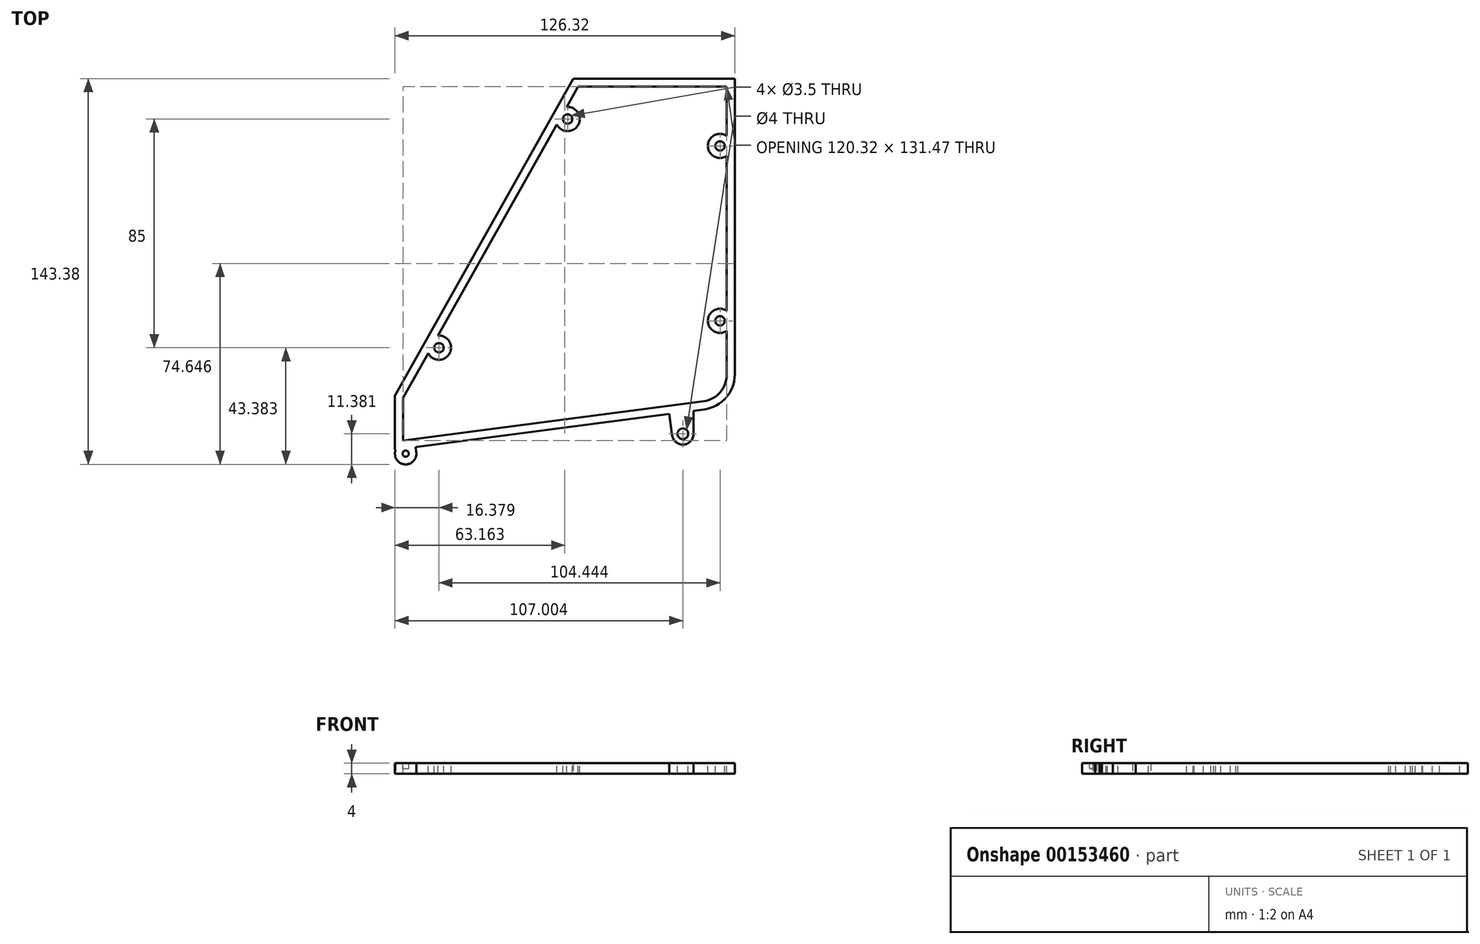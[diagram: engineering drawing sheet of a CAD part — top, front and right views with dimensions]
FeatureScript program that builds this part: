
annotation { "Feature Type Name" : "Feature", "Feature Type Description" : "" }
export const myFeature = defineFeature(function(context is Context, id is Id, definition is map)
    precondition{}
    {
        {
            var Q0;
            Q0=qCreatedBy(makeId("Top.planeOp"),FACE);
            var sketch = newSketch(context, id + "F0", { "sketchPlane" : qUnion([Q0])});
            skLineSegment(sketch, "E0", {"start": v(-60.03, 83.64) * mm, "end": v(-60.03, -26.36) * mm});
            skLineSegment(sketch, "E1", {"start": v(-48.72, -39.25) * mm, "end": v(66.28, -54.25) * mm});
            skLineSegment(sketch, "E2", {"start": v(66.28, -34.25) * mm, "end": v(-0.03, 83.64) * mm});
            skLineSegment(sketch, "E3", {"start": v(-60.03, 83.64) * mm, "end": v(-0.03, 83.64) * mm});
            skLineSegment(sketch, "E4", {"start": v(66.28, -34.25) * mm, "end": v(66.28, -54.25) * mm});
            skPoint(sketch, "E5.visualSharp", {"position": v(-60.03, -37.77) * mm});
            skArc(sketch, "E5.filletArc", {"start": v(-60.03, -26.36) * mm, "mid": v(-56.8, -34.93) * mm, "end": v(-48.72, -39.25) * mm});
            skCircle(sketch, "E6", {"center": v(62.28, -55.74) * mm, "radius": 4 * mm});
            skLineSegment(sketch, "E7", {"start": v(66.28, -55.79) * mm, "end": v(66.28, -54.25) * mm});
            skLineSegment(sketch, "E8", {"start": v(58.37, -54.91) * mm, "end": v(58.59, -53.24) * mm});
            skCircle(sketch, "E9", {"center": v(-40.72, -48.36) * mm, "radius": 4 * mm});
            skLineSegment(sketch, "E10", {"start": v(-44.71, -48.48) * mm, "end": v(-44.71, -39.77) * mm});
            skLineSegment(sketch, "E11", {"start": v(-36.75, -48.88) * mm, "end": v(-35.72, -40.94) * mm});
            skSolve(sketch);
        }
        {
            var Q0;
            {var subQ0=sQuery(id+"F0.wireOp",EDGE,"E7");var subQ1=sQuery(id+"F0.wireOp",EDGE,"E6");var subQ2=makeQuery(id+"F0.imprint","INTERSECT",VERTEX,{"disambiguationData":[OD(0.0)],"derivedFrom":[subQ1,subQ0]});Q0=makeQuery(id+"F0.imprint","IMPRINT",FACE,{"disambiguationData":[TD([[makeQuery(id+"F0.imprint","IMPRINT",EDGE,{"disambiguationData":[TD([[subQ2,-1.0]])],"derivedFrom":subQ1}),1.0]])]});}
            var Q1;
            {var subQ0=sQuery(id+"F0.wireOp",EDGE,"E10");var subQ1=sQuery(id+"F0.wireOp",EDGE,"E9");var subQ2=makeQuery(id+"F0.imprint","INTERSECT",VERTEX,{"disambiguationData":[OD(0.0)],"derivedFrom":[subQ1,subQ0]});Q1=makeQuery(id+"F0.imprint","IMPRINT",FACE,{"disambiguationData":[TD([[makeQuery(id+"F0.imprint","IMPRINT",EDGE,{"disambiguationData":[TD([[subQ2,1.0]])],"derivedFrom":subQ1}),1.0]])]});}
            var Q2;
            {var subQ0=sQuery(id+"F0.wireOp",EDGE,"E10");var subQ1=sQuery(id+"F0.wireOp",EDGE,"E1");var subQ2=makeQuery(id+"F0.imprint","INTERSECT",VERTEX,{"derivedFrom":[subQ1,subQ0]});Q2=makeQuery(id+"F0.imprint","IMPRINT",FACE,{"disambiguationData":[TD([[makeQuery(id+"F0.imprint","IMPRINT",EDGE,{"disambiguationData":[TD([[subQ2,-1.0]])],"derivedFrom":subQ1}),-1.0]])]});}
            var Q3;
            {var subQ0=sQuery(id+"F0.wireOp",EDGE,"E11");Q3=makeQuery(id+"F0.imprint","IMPRINT",FACE,{"disambiguationData":[TD([[makeQuery(id+"F0.imprint","IMPRINT",EDGE,{"derivedFrom":subQ0}),1.0]])]});}
            var Q4;
            {var subQ0=sQuery(id+"F0.wireOp",EDGE,"E8");Q4=makeQuery(id+"F0.imprint","IMPRINT",FACE,{"disambiguationData":[TD([[makeQuery(id+"F0.imprint","IMPRINT",EDGE,{"derivedFrom":subQ0}),-1.0]])]});}
            var Q5;
            {var subQ0=sQuery(id+"F0.wireOp",EDGE,"E7");var subQ3=sQuery(id+"F0.wireOp",EDGE,"E6");var subQ5=makeQuery(id+"F0.imprint","INTERSECT",VERTEX,{"disambiguationData":[OD(1.0)],"derivedFrom":[subQ3,subQ0]});Q5=makeQuery(id+"F0.imprint","IMPRINT",FACE,{"disambiguationData":[TD([[makeQuery(id+"F0.imprint","IMPRINT",EDGE,{"disambiguationData":[TD([[subQ5,-1.0]])],"derivedFrom":subQ3}),-1.0]])]});}
            var Q6;
            {var subQ0=sQuery(id+"F0.wireOp",EDGE,"E9");var subQ2=sQuery(id+"F0.wireOp",EDGE,"E1");var subQ7=makeQuery(id+"F0.imprint","INTERSECT",VERTEX,{"disambiguationData":[OD(0.0)],"derivedFrom":[subQ2,subQ0]});Q6=makeQuery(id+"F0.imprint","IMPRINT",FACE,{"disambiguationData":[TD([[makeQuery(id+"F0.imprint","IMPRINT",EDGE,{"disambiguationData":[TD([[subQ7,-1.0]])],"derivedFrom":subQ2}),-1.0]])]});}
            var Q7;
            {var subQ1=sQuery(id+"F0.wireOp",EDGE,"E6");var subQ4=sQuery(id+"F0.wireOp",EDGE,"E1");var subQ5=makeQuery(id+"F0.imprint","INTERSECT",VERTEX,{"disambiguationData":[OD(0.0)],"derivedFrom":[subQ4,subQ1]});Q7=makeQuery(id+"F0.imprint","IMPRINT",FACE,{"disambiguationData":[TD([[makeQuery(id+"F0.imprint","IMPRINT",EDGE,{"disambiguationData":[TD([[subQ5,-1.0]])],"derivedFrom":subQ4}),-1.0]])]});}
            var Q8;
            {var subQ0=sQuery(id+"F0.wireOp",EDGE,"E6");var subQ1=sQuery(id+"F0.wireOp",EDGE,"E1");var subQ2=makeQuery(id+"F0.imprint","INTERSECT",VERTEX,{"disambiguationData":[OD(0.0)],"derivedFrom":[subQ1,subQ0]});Q8=makeQuery(id+"F0.imprint","IMPRINT",FACE,{"disambiguationData":[TD([[makeQuery(id+"F0.imprint","IMPRINT",EDGE,{"disambiguationData":[TD([[subQ2,-1.0]])],"derivedFrom":subQ1}),1.0]])]});}
            var Q9;
            Q9=makeQuery(id+"F0.imprint","IMPRINT",FACE,{"disambiguationData":[TD([[makeQuery(id+"F0.imprint","IMPRINT",EDGE,{"derivedFrom":sQuery(id+"F0.wireOp",EDGE,"E0")}),1.0]])]});
            var Q10;
            {var subQ0=sQuery(id+"F0.wireOp",EDGE,"E9");var subQ1=sQuery(id+"F0.wireOp",EDGE,"E1");var subQ2=makeQuery(id+"F0.imprint","INTERSECT",VERTEX,{"disambiguationData":[OD(0.0)],"derivedFrom":[subQ1,subQ0]});Q10=makeQuery(id+"F0.imprint","IMPRINT",FACE,{"disambiguationData":[TD([[makeQuery(id+"F0.imprint","IMPRINT",EDGE,{"disambiguationData":[TD([[subQ2,-1.0]])],"derivedFrom":subQ1}),1.0]])]});}
            var Q11;
            {var subQ0=sQuery(id+"F0.wireOp",EDGE,"E10");var subQ1=sQuery(id+"F0.wireOp",EDGE,"E9");var subQ2=makeQuery(id+"F0.imprint","INTERSECT",VERTEX,{"disambiguationData":[OD(0.0)],"derivedFrom":[subQ1,subQ0]});Q11=makeQuery(id+"F0.imprint","IMPRINT",FACE,{"disambiguationData":[TD([[makeQuery(id+"F0.imprint","IMPRINT",EDGE,{"disambiguationData":[TD([[subQ2,-1.0]])],"derivedFrom":subQ1}),1.0]])]});}
            extrude(context, id + "F1", {"entities" : qUnion([Q0, Q1, Q2, Q3, Q4, Q5, Q6, Q7, Q8, Q9, Q10, Q11]), "depth" : 4 * mm});
        }
        {
            var Q0;
            Q0=makeQuery(id+"F1.opExtrude","CAP_FACE",FACE,{"disambiguationData":[OSD([sQuery(id+"F0.wireOp",EDGE,"E0"),sQuery(id+"F0.wireOp",EDGE,"E1"),sQuery(id+"F0.wireOp",EDGE,"E2"),sQuery(id+"F0.wireOp",EDGE,"E3"),sQuery(id+"F0.wireOp",EDGE,"E4"),sQuery(id+"F0.wireOp",EDGE,"E5.filletArc")])],"isStart":false});
            var sketch = newSketch(context, id + "F2", { "sketchPlane" : qUnion([Q0])});
            skLineSegment(sketch, "E12.0", {"start": v(-48.46, -37.26) * mm, "end": v(52.4, -50.42) * mm});
            skArc(sketch, "E12.1", {"start": v(-58.03, -26.36) * mm, "mid": v(-55.3, -33.61) * mm, "end": v(-48.46, -37.26) * mm});
            skLineSegment(sketch, "E12.2", {"start": v(-58.03, 83.64) * mm, "end": v(-58.03, -26.36) * mm});
            skLineSegment(sketch, "E13", {"start": v(66.28, -54.25) * mm, "end": v(66.28, -52.23) * mm});
            skLineSegment(sketch, "E14", {"start": v(-60.03, 83.64) * mm, "end": v(-58.03, 83.64) * mm});
            skLineSegment(sketch, "E15", {"start": v(-48.46, -37.26) * mm, "end": v(-48.72, -39.25) * mm});
            skLineSegment(sketch, "E16.0", {"start": v(59.2, -25.73) * mm, "end": v(-2.7, 84.31) * mm});
            skLineSegment(sketch, "E17", {"start": v(-2.33, 83.64) * mm, "end": v(-2.7, 84.31) * mm});
            skLineSegment(sketch, "E18", {"start": v(59.2, -25.73) * mm, "end": v(66.28, -34.25) * mm});
            skSolve(sketch);
        }
        {
            var Q0;
            Q0=qSketchRegion(id+"F2",true);
            var Q1;
            Q1=makeQuery(id+"F2.imprint","IMPRINT",FACE,{"disambiguationData":[TD([[makeQuery(id+"F2.imprint","IMPRINT",EDGE,{"derivedFrom":sQuery(id+"F2.wireOp",EDGE,"E12.1")}),-1.0]])]});
            var Q2;
            {var subQ2=sQuery(id+"F2.wireOp",EDGE,"E17");Q2=makeQuery(id+"F2.imprint","IMPRINT",FACE,{"disambiguationData":[TD([[makeQuery(id+"F2.imprint","IMPRINT",EDGE,{"derivedFrom":subQ2}),-1.0]])]});}
            var Q3;
            {var subQ0=sQuery(id+"F2.wireOp",EDGE,"E16.0");Q3=makeQuery(id+"F2.imprint","IMPRINT",FACE,{"disambiguationData":[TD([[makeQuery(id+"F2.imprint","IMPRINT",EDGE,{"derivedFrom":subQ0}),-1.0]])]});}
            extrude(context, id + "F3", {"entities" : qUnion([Q0, Q1, Q2, Q3]), "operationType" : NewBodyOperationType.ADD, "depth" : 55 * mm});
        }
        {
            var Q0;
            {var subQ0=sQuery(id+"F0.wireOp",EDGE,"E0");Q0=makeQuery(id+"F3.boolean.opBoolean","MERGE",FACE,{"derivedFrom":[makeQuery(id+"F1.opExtrude","SWEPT_FACE",FACE,{"disambiguationData":[OSD([subQ0])]}),makeQuery(id+"F3.opExtrude","SWEPT_FACE",FACE,{"disambiguationData":[OSD([subQ0])]})]});}
            var sketch = newSketch(context, id + "F4", { "sketchPlane" : qUnion([Q0])});
            skCircle(sketch, "E19", {"center": v(23.36, 41.5) * mm, "radius": 2.5 * mm});
            skCircle(sketch, "E20", {"center": v(-74.64, 41.5) * mm, "radius": 2.5 * mm});
            skSolve(sketch);
        }
        {
            var Q0;
            Q0=qSketchRegion(id+"F4",true);
            extrude(context, id + "F5", {"entities" : qUnion([Q0]), "operationType" : NewBodyOperationType.REMOVE, "endBound" : BoundingType.UP_TO_NEXT, "oppositeDirection" : true, "depth" : 25 * mm});
        }
        {
            var Q0;
            Q0=makeQuery(id+"F1.opExtrude","CAP_FACE",FACE,{"disambiguationData":[OSD([sQuery(id+"F0.wireOp",EDGE,"E0"),sQuery(id+"F0.wireOp",EDGE,"E1"),sQuery(id+"F0.wireOp",EDGE,"E2"),sQuery(id+"F0.wireOp",EDGE,"E3"),sQuery(id+"F0.wireOp",EDGE,"E4"),sQuery(id+"F0.wireOp",EDGE,"E5.filletArc"),sQuery(id+"F0.wireOp",EDGE,"E6"),sQuery(id+"F0.wireOp",EDGE,"E7"),sQuery(id+"F0.wireOp",EDGE,"E8")])],"isStart":false});
            var sketch = newSketch(context, id + "F6", { "sketchPlane" : qUnion([Q0])});
            skCircle(sketch, "E21", {"center": v(62.28, -55.74) * mm, "radius": 1.15 * mm});
            skSolve(sketch);
        }
        {
            var Q0;
            Q0=qSketchRegion(id+"F6",true);
            extrude(context, id + "F7", {"entities" : qUnion([Q0]), "operationType" : NewBodyOperationType.REMOVE, "oppositeDirection" : true, "depth" : 2 * mm});
        }
        {
            var Q0;
            Q0=makeQuery(id+"F3.opExtrude","CAP_FACE",FACE,{"disambiguationData":[OSD([sQuery(id+"F0.wireOp",EDGE,"E0"),sQuery(id+"F0.wireOp",EDGE,"E5.filletArc"),sQuery(id+"F2.wireOp",EDGE,"E12.1"),sQuery(id+"F2.wireOp",EDGE,"E12.2"),sQuery(id+"F2.wireOp",EDGE,"E14"),sQuery(id+"F2.wireOp",EDGE,"E15")])],"isStart":false});
            var sketch = newSketch(context, id + "F8", { "sketchPlane" : qUnion([Q0])});
            skCircle(sketch, "E22", {"center": v(-54.53, -6.36) * mm, "radius": 3.5 * mm});
            skLineSegment(sketch, "E23", {"start": v(-51.48, -4.64) * mm, "end": v(-58.03, 5.64) * mm});
            skLineSegment(sketch, "E24", {"start": v(-52.77, -9.38) * mm, "end": v(-58.03, -12.36) * mm});
            skCircle(sketch, "E25", {"center": v(-54.53, 58.64) * mm, "radius": 3.5 * mm});
            skLineSegment(sketch, "E26", {"start": v(-51.64, 60.61) * mm, "end": v(-58.03, 70.64) * mm});
            skLineSegment(sketch, "E27", {"start": v(-53.23, 55.4) * mm, "end": v(-58.03, 53.64) * mm});
            skSolve(sketch);
        }
        {
            var Q0;
            Q0=qSketchRegion(id+"F8",true);
            var Q1;
            {var subQ0=sQuery(id+"F8.wireOp",EDGE,"E23");Q1=makeQuery(id+"F8.imprint","IMPRINT",FACE,{"disambiguationData":[TD([[makeQuery(id+"F8.imprint","IMPRINT",EDGE,{"derivedFrom":subQ0}),1.0]])]});}
            var Q2;
            {var subQ0=sQuery(id+"F8.wireOp",EDGE,"E24");Q2=makeQuery(id+"F8.imprint","IMPRINT",FACE,{"disambiguationData":[TD([[makeQuery(id+"F8.imprint","IMPRINT",EDGE,{"derivedFrom":subQ0}),-1.0]])]});}
            var Q3;
            {var subQ0=sQuery(id+"F8.wireOp",EDGE,"E26");Q3=makeQuery(id+"F8.imprint","IMPRINT",FACE,{"disambiguationData":[TD([[makeQuery(id+"F8.imprint","IMPRINT",EDGE,{"derivedFrom":subQ0}),1.0]])]});}
            var Q4;
            {var subQ0=sQuery(id+"F8.wireOp",EDGE,"E27");var subQ1=sQuery(id+"F8.wireOp",EDGE,"E25");var subQ2=makeQuery(id+"F8.imprint","INTERSECT",VERTEX,{"disambiguationData":[OD(1.0)],"derivedFrom":[subQ1,subQ0]});Q4=makeQuery(id+"F8.imprint","IMPRINT",FACE,{"disambiguationData":[TD([[makeQuery(id+"F8.imprint","IMPRINT",EDGE,{"disambiguationData":[TD([[subQ2,1.0]])],"derivedFrom":subQ1}),-1.0]])]});}
            extrude(context, id + "F9", {"entities" : qUnion([Q0, Q1, Q2, Q3, Q4]), "operationType" : NewBodyOperationType.ADD, "oppositeDirection" : true, "depth" : 8 * mm});
        }
        {
            var Q0;
            Q0=makeQuery(id+"F3.opExtrude","CAP_FACE",FACE,{"disambiguationData":[OSD([sQuery(id+"F0.wireOp",EDGE,"E2"),sQuery(id+"F0.wireOp",EDGE,"E3"),sQuery(id+"F2.wireOp",EDGE,"E16.0"),sQuery(id+"F2.wireOp",EDGE,"E18")])],"isStart":false});
            var sketch = newSketch(context, id + "F10", { "sketchPlane" : qUnion([Q0])});
            skCircle(sketch, "E28", {"center": v(2.1, 68.64) * mm, "radius": 3.5 * mm});
            skLineSegment(sketch, "E29", {"start": v(-1.4, 68.87) * mm, "end": v(-0.64, 80.64) * mm});
            skLineSegment(sketch, "E30", {"start": v(1.24, 65.25) * mm, "end": v(8.92, 63.64) * mm});
            skCircle(sketch, "E31", {"center": v(49.9, -16.36) * mm, "radius": 3.5 * mm});
            skLineSegment(sketch, "E32", {"start": v(46.47, -15.72) * mm, "end": v(47.17, -4.36) * mm});
            skLineSegment(sketch, "E33", {"start": v(49.2, -19.78) * mm, "end": v(56.74, -21.36) * mm});
            skSolve(sketch);
        }
        {
            var Q0;
            {var subQ0=sQuery(id+"F10.wireOp",EDGE,"E32");var subQ1=sQuery(id+"F10.wireOp",EDGE,"E31");var subQ2=makeQuery(id+"F10.imprint","INTERSECT",VERTEX,{"disambiguationData":[OD(1.0)],"derivedFrom":[subQ1,subQ0]});Q0=makeQuery(id+"F10.imprint","IMPRINT",FACE,{"disambiguationData":[TD([[makeQuery(id+"F10.imprint","IMPRINT",EDGE,{"disambiguationData":[TD([[subQ2,1.0]])],"derivedFrom":subQ1}),1.0]])]});}
            var Q1;
            {var subQ0=sQuery(id+"F10.wireOp",EDGE,"E32");var subQ1=sQuery(id+"F10.wireOp",EDGE,"E31");var subQ2=makeQuery(id+"F10.imprint","INTERSECT",VERTEX,{"disambiguationData":[OD(1.0)],"derivedFrom":[subQ1,subQ0]});Q1=makeQuery(id+"F10.imprint","IMPRINT",FACE,{"disambiguationData":[TD([[makeQuery(id+"F10.imprint","IMPRINT",EDGE,{"disambiguationData":[TD([[subQ2,1.0]])],"derivedFrom":subQ1}),-1.0]])]});}
            var Q2;
            {var subQ0=sQuery(id+"F10.wireOp",EDGE,"E33");Q2=makeQuery(id+"F10.imprint","IMPRINT",FACE,{"disambiguationData":[TD([[makeQuery(id+"F10.imprint","IMPRINT",EDGE,{"derivedFrom":subQ0}),1.0]])]});}
            var Q3;
            {var subQ0=sQuery(id+"F10.wireOp",EDGE,"E28");var subQ1=makeQuery(id+"F10.imprint","INTERSECT",VERTEX,{"derivedFrom":[subQ0,sQuery(id+"F10.wireOp",EDGE,"E29")]});Q3=makeQuery(id+"F10.imprint","IMPRINT",FACE,{"disambiguationData":[TD([[makeQuery(id+"F10.imprint","IMPRINT",EDGE,{"disambiguationData":[TD([[subQ1,1.0]])],"derivedFrom":subQ0}),1.0]])]});}
            var Q4;
            {var subQ0=sQuery(id+"F10.wireOp",EDGE,"E30");var subQ1=sQuery(id+"F10.wireOp",EDGE,"E28");var subQ2=makeQuery(id+"F10.imprint","INTERSECT",VERTEX,{"disambiguationData":[OD(1.0)],"derivedFrom":[subQ1,subQ0]});Q4=makeQuery(id+"F10.imprint","IMPRINT",FACE,{"disambiguationData":[TD([[makeQuery(id+"F10.imprint","IMPRINT",EDGE,{"disambiguationData":[TD([[subQ2,-1.0]])],"derivedFrom":subQ1}),-1.0]])]});}
            var Q5;
            {var subQ0=sQuery(id+"F10.wireOp",EDGE,"E29");Q5=makeQuery(id+"F10.imprint","IMPRINT",FACE,{"disambiguationData":[TD([[makeQuery(id+"F10.imprint","IMPRINT",EDGE,{"derivedFrom":subQ0}),-1.0]])]});}
            extrude(context, id + "F11", {"entities" : qUnion([Q0, Q1, Q2, Q3, Q4, Q5]), "operationType" : NewBodyOperationType.ADD, "oppositeDirection" : true, "depth" : 7 * mm});
        }
        {
            var Q0;
            {var subQ0=sQuery(id+"F2.wireOp",EDGE,"E12.2");Q0=makeQuery(id+"F9.boolean.opBoolean","MERGE",FACE,{"derivedFrom":[makeQuery(id+"F3.opExtrude","CAP_FACE",FACE,{"disambiguationData":[OSD([sQuery(id+"F0.wireOp",EDGE,"E0"),sQuery(id+"F0.wireOp",EDGE,"E5.filletArc"),sQuery(id+"F2.wireOp",EDGE,"E12.1"),subQ0,sQuery(id+"F2.wireOp",EDGE,"E14"),sQuery(id+"F2.wireOp",EDGE,"E15")])],"isStart":false}),makeQuery(id+"F9.opExtrude","CAP_FACE",FACE,{"disambiguationData":[OSD([subQ0,sQuery(id+"F8.wireOp",EDGE,"E22"),sQuery(id+"F8.wireOp",EDGE,"E23"),sQuery(id+"F8.wireOp",EDGE,"E24")])],"isStart":true}),makeQuery(id+"F9.opExtrude","CAP_FACE",FACE,{"disambiguationData":[OSD([subQ0,sQuery(id+"F8.wireOp",EDGE,"E25"),sQuery(id+"F8.wireOp",EDGE,"E26"),sQuery(id+"F8.wireOp",EDGE,"E27")])],"isStart":true})]});}
            var sketch = newSketch(context, id + "F12", { "sketchPlane" : qUnion([Q0])});
            skCircle(sketch, "E34", {"center": v(-54.53, -6.36) * mm, "radius": 1.75 * mm});
            skCircle(sketch, "E35", {"center": v(-54.53, 58.64) * mm, "radius": 1.75 * mm});
            skSolve(sketch);
        }
        {
            var Q0;
            Q0=qSketchRegion(id+"F12",true);
            extrude(context, id + "F13", {"entities" : qUnion([Q0]), "operationType" : NewBodyOperationType.REMOVE, "endBound" : BoundingType.THROUGH_ALL, "oppositeDirection" : true, "depth" : 6.5 * mm});
        }
        {
            var Q0;
            {var subQ0=sQuery(id+"F2.wireOp",EDGE,"E16.0");Q0=makeQuery(id+"F11.boolean.opBoolean","MERGE",FACE,{"derivedFrom":[makeQuery(id+"F3.opExtrude","CAP_FACE",FACE,{"disambiguationData":[OSD([sQuery(id+"F0.wireOp",EDGE,"E2"),sQuery(id+"F0.wireOp",EDGE,"E3"),subQ0,sQuery(id+"F2.wireOp",EDGE,"E18")])],"isStart":false}),makeQuery(id+"F11.opExtrude","CAP_FACE",FACE,{"disambiguationData":[OSD([subQ0,sQuery(id+"F10.wireOp",EDGE,"E28"),sQuery(id+"F10.wireOp",EDGE,"E29"),sQuery(id+"F10.wireOp",EDGE,"E30")])],"isStart":true}),makeQuery(id+"F11.opExtrude","CAP_FACE",FACE,{"disambiguationData":[OSD([subQ0,sQuery(id+"F10.wireOp",EDGE,"E31"),sQuery(id+"F10.wireOp",EDGE,"E32"),sQuery(id+"F10.wireOp",EDGE,"E33")])],"isStart":true})]});}
            var sketch = newSketch(context, id + "F14", { "sketchPlane" : qUnion([Q0])});
            skCircle(sketch, "E36", {"center": v(49.9, -16.36) * mm, "radius": 1.75 * mm});
            skCircle(sketch, "E37", {"center": v(2.1, 68.64) * mm, "radius": 1.75 * mm});
            skSolve(sketch);
        }
        {
            var Q0;
            Q0=qSketchRegion(id+"F14",true);
            extrude(context, id + "F15", {"entities" : qUnion([Q0]), "operationType" : NewBodyOperationType.REMOVE, "endBound" : BoundingType.THROUGH_ALL, "oppositeDirection" : true, "depth" : 6.5 * mm});
        }
        {
            var Q0;
            {var subQ0=sQuery(id+"F2.wireOp",EDGE,"E12.2");Q0=makeQuery(id+"F9.boolean.opBoolean","MERGE",FACE,{"derivedFrom":[makeQuery(id+"F3.opExtrude","CAP_FACE",FACE,{"disambiguationData":[OSD([sQuery(id+"F0.wireOp",EDGE,"E0"),sQuery(id+"F0.wireOp",EDGE,"E5.filletArc"),sQuery(id+"F2.wireOp",EDGE,"E12.1"),subQ0,sQuery(id+"F2.wireOp",EDGE,"E14"),sQuery(id+"F2.wireOp",EDGE,"E15")])],"isStart":false}),makeQuery(id+"F9.opExtrude","CAP_FACE",FACE,{"disambiguationData":[OSD([subQ0,sQuery(id+"F8.wireOp",EDGE,"E22"),sQuery(id+"F8.wireOp",EDGE,"E23"),sQuery(id+"F8.wireOp",EDGE,"E24")])],"isStart":true}),makeQuery(id+"F9.opExtrude","CAP_FACE",FACE,{"disambiguationData":[OSD([subQ0,sQuery(id+"F8.wireOp",EDGE,"E25"),sQuery(id+"F8.wireOp",EDGE,"E26"),sQuery(id+"F8.wireOp",EDGE,"E27")])],"isStart":true})]});}
            extrude(context, id + "F16", {"entities" : qUnion([Q0]), "operationType" : NewBodyOperationType.REMOVE, "oppositeDirection" : true, "depth" : 55 * mm});
        }
        {
            var Q0;
            {var subQ0=sQuery(id+"F2.wireOp",EDGE,"E16.0");Q0=makeQuery(id+"F11.boolean.opBoolean","MERGE",FACE,{"derivedFrom":[makeQuery(id+"F3.opExtrude","CAP_FACE",FACE,{"disambiguationData":[OSD([sQuery(id+"F0.wireOp",EDGE,"E2"),sQuery(id+"F0.wireOp",EDGE,"E3"),subQ0,sQuery(id+"F2.wireOp",EDGE,"E18")])],"isStart":false}),makeQuery(id+"F11.opExtrude","CAP_FACE",FACE,{"disambiguationData":[OSD([subQ0,sQuery(id+"F10.wireOp",EDGE,"E28"),sQuery(id+"F10.wireOp",EDGE,"E29"),sQuery(id+"F10.wireOp",EDGE,"E30")])],"isStart":true}),makeQuery(id+"F11.opExtrude","CAP_FACE",FACE,{"disambiguationData":[OSD([subQ0,sQuery(id+"F10.wireOp",EDGE,"E31"),sQuery(id+"F10.wireOp",EDGE,"E32"),sQuery(id+"F10.wireOp",EDGE,"E33")])],"isStart":true})]});}
            var Q1;
            {var subQ0=sQuery(id+"F0.wireOp",EDGE,"E5.filletArc");var subQ1=sQuery(id+"F0.wireOp",EDGE,"E0");Q1=makeQuery(id+"F16.boolean.opBoolean","MERGE",FACE,{"derivedFrom":[makeQuery(id+"F1.opExtrude","CAP_FACE",FACE,{"disambiguationData":[OSD([subQ1,sQuery(id+"F0.wireOp",EDGE,"E1"),sQuery(id+"F0.wireOp",EDGE,"E2"),sQuery(id+"F0.wireOp",EDGE,"E3"),sQuery(id+"F0.wireOp",EDGE,"E4"),subQ0,sQuery(id+"F0.wireOp",EDGE,"E6"),sQuery(id+"F0.wireOp",EDGE,"E7"),sQuery(id+"F0.wireOp",EDGE,"E8"),sQuery(id+"F0.wireOp",EDGE,"E9"),sQuery(id+"F0.wireOp",EDGE,"E10"),sQuery(id+"F0.wireOp",EDGE,"E11")])],"isStart":false}),makeQuery(id+"F16.opExtrude","CAP_FACE",FACE,{"disambiguationData":[OSD([subQ1,subQ0,sQuery(id+"F2.wireOp",EDGE,"E12.1"),sQuery(id+"F2.wireOp",EDGE,"E12.2"),sQuery(id+"F2.wireOp",EDGE,"E14"),sQuery(id+"F2.wireOp",EDGE,"E15"),sQuery(id+"F8.wireOp",EDGE,"E22"),sQuery(id+"F8.wireOp",EDGE,"E23"),sQuery(id+"F8.wireOp",EDGE,"E24"),sQuery(id+"F8.wireOp",EDGE,"E25"),sQuery(id+"F8.wireOp",EDGE,"E26"),sQuery(id+"F8.wireOp",EDGE,"E27")])],"isStart":false})]});}
            extrude(context, id + "F17", {"entities" : qUnion([Q0]), "operationType" : NewBodyOperationType.REMOVE, "endBound" : BoundingType.UP_TO_SURFACE, "oppositeDirection" : true, "endBoundEntityFace" : qUnion([Q1]), "depth" : 55 * mm});
        }
        {
            var Q0;
            Q0=makeQuery(id+"F1.opExtrude","SWEPT_BODY",BODY,{"disambiguationData":[OSD([sQuery(id+"F0.wireOp",EDGE,"E0"),sQuery(id+"F0.wireOp",EDGE,"E1"),sQuery(id+"F0.wireOp",EDGE,"E2"),sQuery(id+"F0.wireOp",EDGE,"E3"),sQuery(id+"F0.wireOp",EDGE,"E4"),sQuery(id+"F0.wireOp",EDGE,"E5.filletArc"),sQuery(id+"F0.wireOp",EDGE,"E6"),sQuery(id+"F0.wireOp",EDGE,"E7"),sQuery(id+"F0.wireOp",EDGE,"E8"),sQuery(id+"F0.wireOp",EDGE,"E9"),sQuery(id+"F0.wireOp",EDGE,"E10"),sQuery(id+"F0.wireOp",EDGE,"E11")])]});
            var Q1;
            Q1=makeQuery(id+"F1.opExtrude","SWEPT_FACE",FACE,{"disambiguationData":[OSD([sQuery(id+"F0.wireOp",EDGE,"E4")])]});
            mirror(context, id + "F18", {"entities" : qUnion([Q0]), "mirrorPlane" : qUnion([Q1])});
        }
        {
            var Q0;
            Q0=makeQuery(id+"F1.opExtrude","SWEPT_BODY",BODY,{"disambiguationData":[OSD([sQuery(id+"F0.wireOp",EDGE,"E0"),sQuery(id+"F0.wireOp",EDGE,"E1"),sQuery(id+"F0.wireOp",EDGE,"E2"),sQuery(id+"F0.wireOp",EDGE,"E3"),sQuery(id+"F0.wireOp",EDGE,"E4"),sQuery(id+"F0.wireOp",EDGE,"E5.filletArc"),sQuery(id+"F0.wireOp",EDGE,"E6"),sQuery(id+"F0.wireOp",EDGE,"E7"),sQuery(id+"F0.wireOp",EDGE,"E8"),sQuery(id+"F0.wireOp",EDGE,"E9"),sQuery(id+"F0.wireOp",EDGE,"E10"),sQuery(id+"F0.wireOp",EDGE,"E11")])]});
            deleteBodies(context, id + "F19", {"entities" : qUnion([Q0])});
        }
        {
            var Q0;
            {var subQ0=sQuery(id+"F8.wireOp",EDGE,"E27");var subQ1=sQuery(id+"F8.wireOp",EDGE,"E26");var subQ2=sQuery(id+"F8.wireOp",EDGE,"E25");var subQ3=sQuery(id+"F8.wireOp",EDGE,"E24");var subQ4=sQuery(id+"F8.wireOp",EDGE,"E23");var subQ5=sQuery(id+"F8.wireOp",EDGE,"E22");var subQ6=sQuery(id+"F2.wireOp",EDGE,"E15");var subQ7=sQuery(id+"F2.wireOp",EDGE,"E14");var subQ8=sQuery(id+"F2.wireOp",EDGE,"E12.2");var subQ9=sQuery(id+"F2.wireOp",EDGE,"E12.1");var subQ10=sQuery(id+"F0.wireOp",EDGE,"E11");var subQ11=sQuery(id+"F0.wireOp",EDGE,"E10");var subQ12=sQuery(id+"F0.wireOp",EDGE,"E9");var subQ13=sQuery(id+"F0.wireOp",EDGE,"E8");var subQ14=sQuery(id+"F0.wireOp",EDGE,"E7");var subQ15=sQuery(id+"F0.wireOp",EDGE,"E6");var subQ16=sQuery(id+"F0.wireOp",EDGE,"E5.filletArc");var subQ17=sQuery(id+"F0.wireOp",EDGE,"E4");var subQ18=sQuery(id+"F0.wireOp",EDGE,"E3");var subQ19=sQuery(id+"F0.wireOp",EDGE,"E2");var subQ20=sQuery(id+"F0.wireOp",EDGE,"E1");var subQ21=sQuery(id+"F0.wireOp",EDGE,"E0");Q0=makeQuery(id+"F18.opPattern","COPY",FACE,{"derivedFrom":makeQuery(id+"F17.boolean.opBoolean","MERGE",FACE,{"derivedFrom":[makeQuery(id+"F16.boolean.opBoolean","MERGE",FACE,{"derivedFrom":[makeQuery(id+"F1.opExtrude","CAP_FACE",FACE,{"disambiguationData":[OSD([subQ21,subQ20,subQ19,subQ18,subQ17,subQ16,subQ15,subQ14,subQ13,subQ12,subQ11,subQ10])],"isStart":false}),makeQuery(id+"F16.opExtrude","CAP_FACE",FACE,{"disambiguationData":[OSD([subQ21,subQ16,subQ9,subQ8,subQ7,subQ6,subQ5,subQ4,subQ3,subQ2,subQ1,subQ0])],"isStart":false})]}),makeQuery(id+"F17.opExtrude","CAP_FACE",FACE,{"disambiguationData":[OSD([subQ21,subQ20,subQ19,subQ18,subQ17,subQ16,subQ15,subQ14,subQ13,subQ12,subQ11,subQ10,subQ9,subQ8,subQ7,subQ6,subQ5,subQ4,subQ3,subQ2,subQ1,subQ0])],"isStart":false})]}),"instanceName":"1"});}
            var sketch = newSketch(context, id + "F20", { "sketchPlane" : qUnion([Q0])});
            skCircle(sketch, "E38", {"center": v(173.28, -48.36) * mm, "radius": 2 * mm});
            skSolve(sketch);
        }
        {
            var Q0;
            Q0=qSketchRegion(id+"F20",true);
            extrude(context, id + "F21", {"entities" : qUnion([Q0]), "operationType" : NewBodyOperationType.REMOVE, "endBound" : BoundingType.UP_TO_NEXT, "oppositeDirection" : true, "depth" : 25 * mm});
        }
        {
            var Q0;
            {var subQ0=sQuery(id+"F8.wireOp",EDGE,"E27");var subQ1=sQuery(id+"F8.wireOp",EDGE,"E26");var subQ2=sQuery(id+"F8.wireOp",EDGE,"E25");var subQ3=sQuery(id+"F8.wireOp",EDGE,"E24");var subQ4=sQuery(id+"F8.wireOp",EDGE,"E23");var subQ5=sQuery(id+"F8.wireOp",EDGE,"E22");var subQ6=sQuery(id+"F2.wireOp",EDGE,"E15");var subQ7=sQuery(id+"F2.wireOp",EDGE,"E14");var subQ8=sQuery(id+"F2.wireOp",EDGE,"E12.2");var subQ9=sQuery(id+"F2.wireOp",EDGE,"E12.1");var subQ10=sQuery(id+"F0.wireOp",EDGE,"E11");var subQ11=sQuery(id+"F0.wireOp",EDGE,"E10");var subQ12=sQuery(id+"F0.wireOp",EDGE,"E9");var subQ13=sQuery(id+"F0.wireOp",EDGE,"E8");var subQ14=sQuery(id+"F0.wireOp",EDGE,"E7");var subQ15=sQuery(id+"F0.wireOp",EDGE,"E6");var subQ16=sQuery(id+"F0.wireOp",EDGE,"E5.filletArc");var subQ17=sQuery(id+"F0.wireOp",EDGE,"E4");var subQ18=sQuery(id+"F0.wireOp",EDGE,"E3");var subQ19=sQuery(id+"F0.wireOp",EDGE,"E2");var subQ20=sQuery(id+"F0.wireOp",EDGE,"E1");var subQ21=sQuery(id+"F0.wireOp",EDGE,"E0");Q0=makeQuery(id+"F18.opPattern","COPY",FACE,{"derivedFrom":makeQuery(id+"F17.boolean.opBoolean","MERGE",FACE,{"derivedFrom":[makeQuery(id+"F16.boolean.opBoolean","MERGE",FACE,{"derivedFrom":[makeQuery(id+"F1.opExtrude","CAP_FACE",FACE,{"disambiguationData":[OSD([subQ21,subQ20,subQ19,subQ18,subQ17,subQ16,subQ15,subQ14,subQ13,subQ12,subQ11,subQ10])],"isStart":false}),makeQuery(id+"F16.opExtrude","CAP_FACE",FACE,{"disambiguationData":[OSD([subQ21,subQ16,subQ9,subQ8,subQ7,subQ6,subQ5,subQ4,subQ3,subQ2,subQ1,subQ0])],"isStart":false})]}),makeQuery(id+"F17.opExtrude","CAP_FACE",FACE,{"disambiguationData":[OSD([subQ21,subQ20,subQ19,subQ18,subQ17,subQ16,subQ15,subQ14,subQ13,subQ12,subQ11,subQ10,subQ9,subQ8,subQ7,subQ6,subQ5,subQ4,subQ3,subQ2,subQ1,subQ0])],"isStart":false})]}),"instanceName":"1"});}
            var sketch = newSketch(context, id + "F22", { "sketchPlane" : qUnion([Q0])});
            skLineSegment(sketch, "E39.0", {"start": v(69.28, -35.03) * mm, "end": v(69.28, -54.25) * mm});
            skLineSegment(sketch, "E39.1", {"start": v(135.22, 82.17) * mm, "end": v(69.28, -35.03) * mm});
            skLineSegment(sketch, "E40.0", {"start": v(180.9, -36.27) * mm, "end": v(176.9, -36.8) * mm});
            skArc(sketch, "E40.1", {"start": v(189.6, -26.36) * mm, "mid": v(187.12, -32.95) * mm, "end": v(180.9, -36.27) * mm});
            skLineSegment(sketch, "E40.2", {"start": v(189.6, 83.64) * mm, "end": v(189.6, -26.36) * mm});
            skLineSegment(sketch, "E41.0", {"start": v(163.97, -46.55) * mm, "end": v(164.36, -49.52) * mm});
            skLineSegment(sketch, "E41.1", {"start": v(79.09, -57.62) * mm, "end": v(163.97, -46.55) * mm});
            skArc(sketch, "E41.2", {"start": v(61.28, -55.68) * mm, "mid": v(69.3, -64.69) * mm, "end": v(79.09, -57.62) * mm});
            skLineSegment(sketch, "E41.3", {"start": v(61.28, -54.25) * mm, "end": v(61.28, -55.68) * mm});
            skLineSegment(sketch, "E41.4", {"start": v(61.28, -32.94) * mm, "end": v(61.28, -54.25) * mm});
            skArc(sketch, "E41.5", {"start": v(164.36, -49.52) * mm, "mid": v(173.96, -57.33) * mm, "end": v(182.28, -48.18) * mm});
            skLineSegment(sketch, "E41.6", {"start": v(182.28, -48.18) * mm, "end": v(182.28, -44.16) * mm});
            skArc(sketch, "E41.7", {"start": v(182.28, -44.16) * mm, "mid": v(193.24, -38.1) * mm, "end": v(197.6, -26.36) * mm});
            skLineSegment(sketch, "E41.8", {"start": v(197.6, -26.36) * mm, "end": v(197.6, 88.64) * mm});
            skLineSegment(sketch, "E41.9", {"start": v(197.6, 88.64) * mm, "end": v(129.68, 88.64) * mm});
            skLineSegment(sketch, "E41.10", {"start": v(129.68, 88.64) * mm, "end": v(61.28, -32.94) * mm});
            skLineSegment(sketch, "E42.0", {"start": v(192.6, 80.64) * mm, "end": v(132.6, 80.64) * mm});
            skLineSegment(sketch, "E43.0", {"start": v(167.9, -37.97) * mm, "end": v(73.6, -50.27) * mm});
            skLineSegment(sketch, "E44", {"start": v(167.9, -37.97) * mm, "end": v(176.9, -36.8) * mm});
            skLineSegment(sketch, "E45", {"start": v(73.6, -50.27) * mm, "end": v(69.28, -50.83) * mm});
            skCircle(sketch, "E46", {"center": v(82.66, -16.36) * mm, "radius": 4.5 * mm});
            skCircle(sketch, "E47", {"center": v(187.1, -6.36) * mm, "radius": 4.5 * mm});
            skCircle(sketch, "E48", {"center": v(187.1, 58.64) * mm, "radius": 4.5 * mm});
            skCircle(sketch, "E49", {"center": v(130.47, 68.64) * mm, "radius": 4.5 * mm});
            skSolve(sketch);
        }
        {
            var Q0;
            Q0=makeQuery(id+"F22.imprint","IMPRINT",FACE,{"disambiguationData":[TD([[makeQuery(id+"F22.imprint","IMPRINT",EDGE,{"derivedFrom":sQuery(id+"F22.wireOp",EDGE,"E40.0")}),-1.0]])]});
            extrude(context, id + "F23", {"entities" : qUnion([Q0]), "operationType" : NewBodyOperationType.REMOVE, "endBound" : BoundingType.UP_TO_NEXT, "oppositeDirection" : true, "depth" : 25 * mm});
        }
    });
